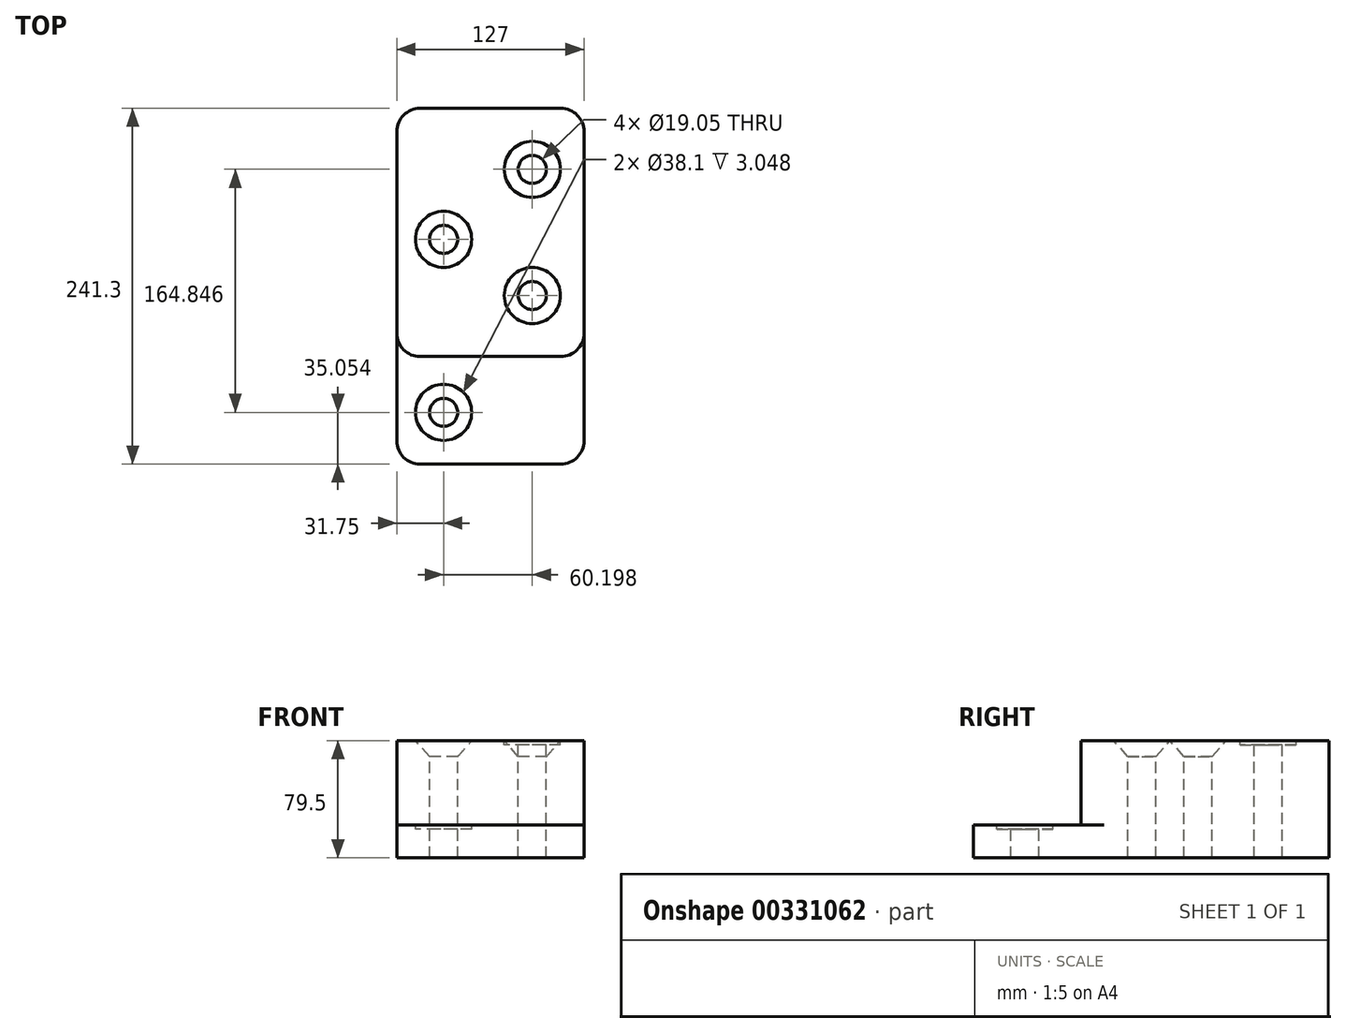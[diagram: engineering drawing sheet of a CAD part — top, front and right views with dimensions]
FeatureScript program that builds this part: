
annotation { "Feature Type Name" : "Feature", "Feature Type Description" : "" }
export const myFeature = defineFeature(function(context is Context, id is Id, definition is map)
    precondition{}
    {
        {
            var Q0;
            Q0=qCreatedBy(makeId("Top.planeOp"),FACE);
            var sketch = newSketch(context, id + "F0", { "sketchPlane" : qUnion([Q0])});
            skLineSegment(sketch, "E0.bottom", {"start": v(-47.75, 0) * mm, "end": v(47.75, 0) * mm});
            skLineSegment(sketch, "E0.top", {"start": v(-47.75, -72.9) * mm, "end": v(47.75, -72.9) * mm});
            skLineSegment(sketch, "E0.left", {"start": v(-63.5, 0) * mm, "end": v(-63.5, -57.15) * mm});
            skLineSegment(sketch, "E0.right", {"start": v(63.5, 0) * mm, "end": v(63.5, -57.15) * mm});
            skLineSegment(sketch, "E1.top", {"start": v(-47.75, 168.4) * mm, "end": v(47.75, 168.4) * mm});
            skLineSegment(sketch, "E1.left", {"start": v(-63.5, 0) * mm, "end": v(-63.5, 152.65) * mm});
            skLineSegment(sketch, "E1.right", {"start": v(63.5, 0) * mm, "end": v(63.5, 152.65) * mm});
            skPoint(sketch, "E2", {"position": v(-31.75, -37.85) * mm});
            skPoint(sketch, "E3", {"position": v(-31.75, 79.5) * mm});
            skPoint(sketch, "E4", {"position": v(28.45, 127) * mm});
            skPoint(sketch, "E5", {"position": v(28.45, 41.4) * mm});
            skArc(sketch, "E6", {"start": v(-63.5, -57.15) * mm, "mid": v(-58.89, -68.29) * mm, "end": v(-47.75, -72.9) * mm});
            skArc(sketch, "E7", {"start": v(47.75, -72.9) * mm, "mid": v(58.89, -68.29) * mm, "end": v(63.5, -57.15) * mm});
            skArc(sketch, "E8", {"start": v(-63.5, 15.75) * mm, "mid": v(-58.89, 4.61) * mm, "end": v(-47.75, 0) * mm});
            skArc(sketch, "E9", {"start": v(47.75, 0) * mm, "mid": v(58.89, 4.61) * mm, "end": v(63.5, 15.75) * mm});
            skArc(sketch, "E10", {"start": v(63.5, 152.65) * mm, "mid": v(58.89, 163.79) * mm, "end": v(47.75, 168.4) * mm});
            skArc(sketch, "E11", {"start": v(-47.75, 168.4) * mm, "mid": v(-58.89, 163.79) * mm, "end": v(-63.5, 152.65) * mm});
            skPoint(sketch, "E12.orphan", {"position": v(63.5, 168.4) * mm});
            skPoint(sketch, "E13.orphan", {"position": v(-63.5, -72.9) * mm});
            skPoint(sketch, "E14.orphan", {"position": v(63.5, -72.9) * mm});
            skSolve(sketch);
        }
        {
            var Q0;
            Q0=makeQuery(id+"F0.imprint","IMPRINT",FACE,{"disambiguationData":[TD([[makeQuery(id+"F0.imprint","IMPRINT",EDGE,{"derivedFrom":sQuery(id+"F0.wireOp",EDGE,"E0.bottom")}),1.0]])]});
            extrude(context, id + "F1", {"entities" : qUnion([Q0]), "depth" : 79.5 * mm});
        }
        {
            var Q0;
            Q0=makeQuery(id+"F0.imprint","IMPRINT",FACE,{"disambiguationData":[TD([[makeQuery(id+"F0.imprint","IMPRINT",EDGE,{"derivedFrom":sQuery(id+"F0.wireOp",EDGE,"E0.top")}),1.0]])]});
            extrude(context, id + "F2", {"entities" : qUnion([Q0]), "operationType" : NewBodyOperationType.ADD, "depth" : 22.35 * mm});
        }
        {
            var Q0;
            Q0=makeQuery(id+"F2.opExtrude","CAP_FACE",FACE,{"disambiguationData":[OSD([sQuery(id+"F0.wireOp",EDGE,"E0.top"),sQuery(id+"F0.wireOp",EDGE,"E0.left"),sQuery(id+"F0.wireOp",EDGE,"E0.right"),sQuery(id+"F0.wireOp",EDGE,"E0.bottom"),sQuery(id+"F0.wireOp",EDGE,"E1.left"),sQuery(id+"F0.wireOp",EDGE,"E1.right"),sQuery(id+"F0.wireOp",EDGE,"E6"),sQuery(id+"F0.wireOp",EDGE,"E7"),sQuery(id+"F0.wireOp",EDGE,"E8"),sQuery(id+"F0.wireOp",EDGE,"E9")])],"isStart":false});
            var sketch = newSketch(context, id + "F3", { "sketchPlane" : qUnion([Q0])});
            skPoint(sketch, "E15.0", {"position": v(-31.75, -37.85) * mm});
            skSolve(sketch);
        }
        {
            var Q0;
            Q0=makeQuery(id+"F1.opExtrude","CAP_FACE",FACE,{"disambiguationData":[OSD([sQuery(id+"F0.wireOp",EDGE,"E0.bottom"),sQuery(id+"F0.wireOp",EDGE,"E1.top"),sQuery(id+"F0.wireOp",EDGE,"E1.left"),sQuery(id+"F0.wireOp",EDGE,"E1.right"),sQuery(id+"F0.wireOp",EDGE,"E8"),sQuery(id+"F0.wireOp",EDGE,"E9"),sQuery(id+"F0.wireOp",EDGE,"E10"),sQuery(id+"F0.wireOp",EDGE,"E11")])],"isStart":false});
            var sketch = newSketch(context, id + "F4", { "sketchPlane" : qUnion([Q0])});
            skPoint(sketch, "E16.0", {"position": v(28.45, 41.4) * mm});
            skPoint(sketch, "E16.1", {"position": v(-31.75, 79.5) * mm});
            skPoint(sketch, "E16.2", {"position": v(28.45, 127) * mm});
            skSolve(sketch);
        }
        {
            var Q0;
            Q0=sQuery(id+"F4.wireOp",VERTEX,"E16.2");
            var Q1;
            Q1=sQuery(id+"F3.wireOp",VERTEX,"E15.0");
            var Q2;
            Q2=makeQuery(id+"F1.opExtrude","SWEPT_BODY",BODY,{"disambiguationData":[OSD([sQuery(id+"F0.wireOp",EDGE,"E0.bottom"),sQuery(id+"F0.wireOp",EDGE,"E1.top"),sQuery(id+"F0.wireOp",EDGE,"E1.left"),sQuery(id+"F0.wireOp",EDGE,"E1.right"),sQuery(id+"F0.wireOp",EDGE,"E8"),sQuery(id+"F0.wireOp",EDGE,"E9"),sQuery(id+"F0.wireOp",EDGE,"E10"),sQuery(id+"F0.wireOp",EDGE,"E11")])]});
            hole(context, id + "F5", {"style" : HoleStyle.C_BORE, "endStyle" : HoleEndStyle.THROUGH, "holeDiameter" : 19.05 * mm, "cBoreDiameter" : 38.1 * mm, "cBoreDepth" : 3.05 * mm, "tappedDepth" : 12.7 * mm, "tapClearance" : 3, "locations" : qUnion([Q0, Q1]), "scope" : qUnion([Q2])});
        }
        {
            var Q0;
            Q0=sQuery(id+"F4.wireOp",VERTEX,"E16.1");
            var Q1;
            Q1=sQuery(id+"F4.wireOp",VERTEX,"E16.0");
            var Q2;
            Q2=makeQuery(id+"F1.opExtrude","SWEPT_BODY",BODY,{"disambiguationData":[OSD([sQuery(id+"F0.wireOp",EDGE,"E0.bottom"),sQuery(id+"F0.wireOp",EDGE,"E1.top"),sQuery(id+"F0.wireOp",EDGE,"E1.left"),sQuery(id+"F0.wireOp",EDGE,"E1.right"),sQuery(id+"F0.wireOp",EDGE,"E8"),sQuery(id+"F0.wireOp",EDGE,"E9"),sQuery(id+"F0.wireOp",EDGE,"E10"),sQuery(id+"F0.wireOp",EDGE,"E11")])]});
            hole(context, id + "F6", {"style" : HoleStyle.C_SINK, "endStyle" : HoleEndStyle.THROUGH, "holeDiameter" : 19.05 * mm, "cSinkDiameter" : 38.1 * mm, "cSinkAngle" : 82 * degree, "tappedDepth" : 12.7 * mm, "tapClearance" : 3, "locations" : qUnion([Q0, Q1]), "scope" : qUnion([Q2])});
        }
    });
